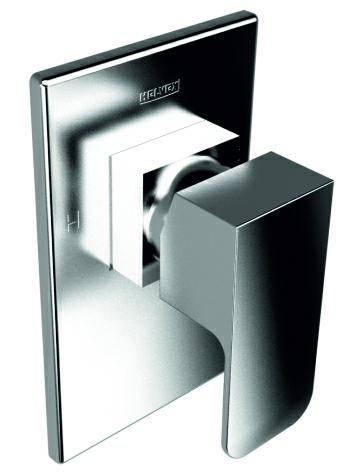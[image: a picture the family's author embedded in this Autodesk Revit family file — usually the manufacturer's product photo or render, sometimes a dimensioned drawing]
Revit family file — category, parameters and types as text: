
# Revit family: Monomando de Regadera E-710
name_source: partatom
category: Plumbing Fixtures
revit_build: Autodesk Revit 2015 (Build: 20140223_1515(x64)
units: mm (PartAtom-declared; Revit-internal decimal feet)

## types (1)
- E-793
    Brass Chromed = Brass
    Cartucho = Cartucho monomando cerámico con balanceo de presión Ø40mm
    Default Elevation = 1"
    Description = Monomando para Regadera o Tina sin Desviador.
    Garantía = El producto HELVEX está garantizado como libre de defectos en materiales y procesos de fabricación. El producto HELVEX está garantizado, en lo que se refiere a los acabados; por un periodo de 10 años en los acabados cromo y duravex, y por 2 años en cabados diferentes al cromo, a partir de la fecha de compra indicada en la factura.
    Instalación = ½" - 14 NPT
    Manufacturer = HELVEX S.A. DE C.V.
    Model = E-710
    Operación = Para abrir el flujo de agua levante la palanca maneral y gire para regular la temperatura.
    Presión máxima de trabajo = 85.3 psi
    Presión mínima de trabajo = 14.2 psi
    Satin = Satín
    Support Base Diameter = 5"
    Total Height = 6"
    Type Comments = Monomando Squadra
    Type Image = E-710.jpg
    URL = http://www.helvex.com.mx

## geometry (parser evidence)
native form markers: Sweep x3
no freeform markers — native parametric forms only
